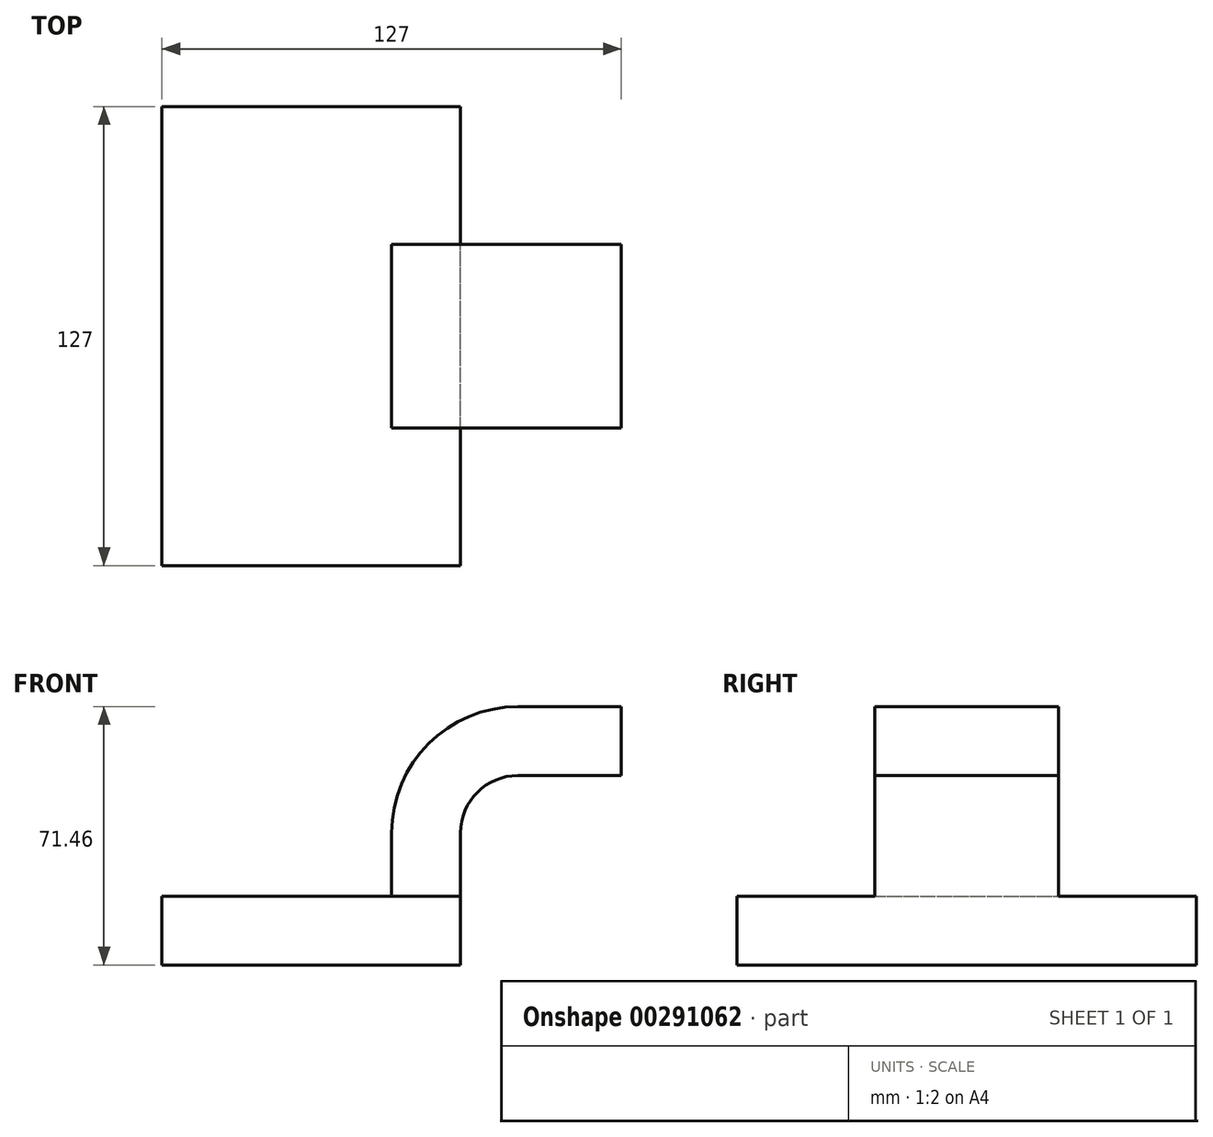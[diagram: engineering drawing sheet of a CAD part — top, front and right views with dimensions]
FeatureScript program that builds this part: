
annotation { "Feature Type Name" : "Feature", "Feature Type Description" : "" }
export const myFeature = defineFeature(function(context is Context, id is Id, definition is map)
    precondition{}
    {
        {
            var Q0;
            Q0=qCreatedBy(makeId("Front.planeOp"),FACE);
            var sketch = newSketch(context, id + "F0", { "sketchPlane" : qUnion([Q0])});
            skLineSegment(sketch, "E0.bottom", {"start": v(41.28, -9.52) * mm, "end": v(-41.28, -9.53) * mm});
            skLineSegment(sketch, "E0.top", {"start": v(41.28, 9.52) * mm, "end": v(-41.28, 9.52) * mm});
            skLineSegment(sketch, "E0.left", {"start": v(41.28, -9.52) * mm, "end": v(41.28, 9.53) * mm});
            skLineSegment(sketch, "E0.right", {"start": v(-41.28, -9.53) * mm, "end": v(-41.28, 9.52) * mm});
            skPoint(sketch, "E0.middle", {"position": v(0, 0) * mm});
            skLineSegment(sketch, "E1.bottom", {"start": v(60.33, 38.1) * mm, "end": v(111.12, 38.1) * mm});
            skLineSegment(sketch, "E1.top", {"start": v(60.33, 66.68) * mm, "end": v(111.13, 66.68) * mm});
            skLineSegment(sketch, "E1.left", {"start": v(60.33, 38.1) * mm, "end": v(60.33, 66.68) * mm});
            skLineSegment(sketch, "E1.right", {"start": v(111.12, 38.1) * mm, "end": v(111.12, 66.68) * mm});
            skPoint(sketch, "E1.middle", {"position": v(85.72, 52.39) * mm});
            skLineSegment(sketch, "E2", {"start": v(41.28, 9.52) * mm, "end": v(41.28, 27) * mm});
            skArc(sketch, "E3", {"start": v(41.28, 27) * mm, "mid": v(45.92, 38.23) * mm, "end": v(57.15, 42.88) * mm});
            skLineSegment(sketch, "E4", {"start": v(57.15, 42.88) * mm, "end": v(85.72, 42.88) * mm});
            skLineSegment(sketch, "E5.0", {"start": v(57.15, 61.93) * mm, "end": v(85.72, 61.93) * mm});
            skArc(sketch, "E5.1", {"start": v(22.23, 27) * mm, "mid": v(32.45, 51.7) * mm, "end": v(57.15, 61.93) * mm});
            skLineSegment(sketch, "E5.2", {"start": v(22.22, 9.52) * mm, "end": v(22.22, 27) * mm});
            skLineSegment(sketch, "E6", {"start": v(85.72, 38.1) * mm, "end": v(85.72, 66.68) * mm});
            skFitSpline(sketch, "E7", {"points": [v(-41.28, 9.53) * mm, v(57.15, 61.93) * mm], "startDerivative": vector(1.6, 140.08) * mm, "endDerivative": vector(151.77, -3.27) * mm});
            skSolve(sketch);
        }
        {
            var Q0;
            Q0=makeQuery(id+"F0.imprint","IMPRINT",FACE,{"disambiguationData":[TD([[makeQuery(id+"F0.imprint","IMPRINT",EDGE,{"derivedFrom":sQuery(id+"F0.wireOp",EDGE,"E0.bottom")}),-1.0]])]});
            extrude(context, id + "F1", {"entities" : qUnion([Q0]), "endBound" : BoundingType.SYMMETRIC, "depth" : 127 * mm});
        }
        {
            var Q0;
            {var subQ1=sQuery(id+"F0.wireOp",EDGE,"E2");Q0=makeQuery(id+"F0.imprint","IMPRINT",FACE,{"disambiguationData":[TD([[makeQuery(id+"F0.imprint","IMPRINT",EDGE,{"derivedFrom":subQ1}),1.0]])]});}
            var Q1;
            {var subQ0=sQuery(id+"F0.wireOp",EDGE,"E4");var subQ1=sQuery(id+"F0.wireOp",EDGE,"E1.left");var subQ2=makeQuery(id+"F0.imprint","INTERSECT",VERTEX,{"derivedFrom":[subQ1,subQ0]});Q1=makeQuery(id+"F0.imprint","IMPRINT",FACE,{"disambiguationData":[TD([[makeQuery(id+"F0.imprint","IMPRINT",EDGE,{"disambiguationData":[TD([[subQ2,-1.0]])],"derivedFrom":subQ1}),-1.0]])]});}
            extrude(context, id + "F2", {"entities" : qUnion([Q0, Q1]), "operationType" : NewBodyOperationType.ADD, "endBound" : BoundingType.SYMMETRIC, "depth" : 50.8 * mm});
        }
        {
            var Q0;
            Q0=makeQuery(id+"F0.imprint","IMPRINT",FACE,{"disambiguationData":[TD([[makeQuery(id+"F0.imprint","IMPRINT",EDGE,{"derivedFrom":sQuery(id+"F0.wireOp",EDGE,"E5.1")}),1.0]])]});
            extrude(context, id + "F3", {"entities" : qUnion([Q0]), "operationType" : NewBodyOperationType.ADD, "endBound" : BoundingType.SYMMETRIC, "depth" : 15.88 * mm});
        }
    });
